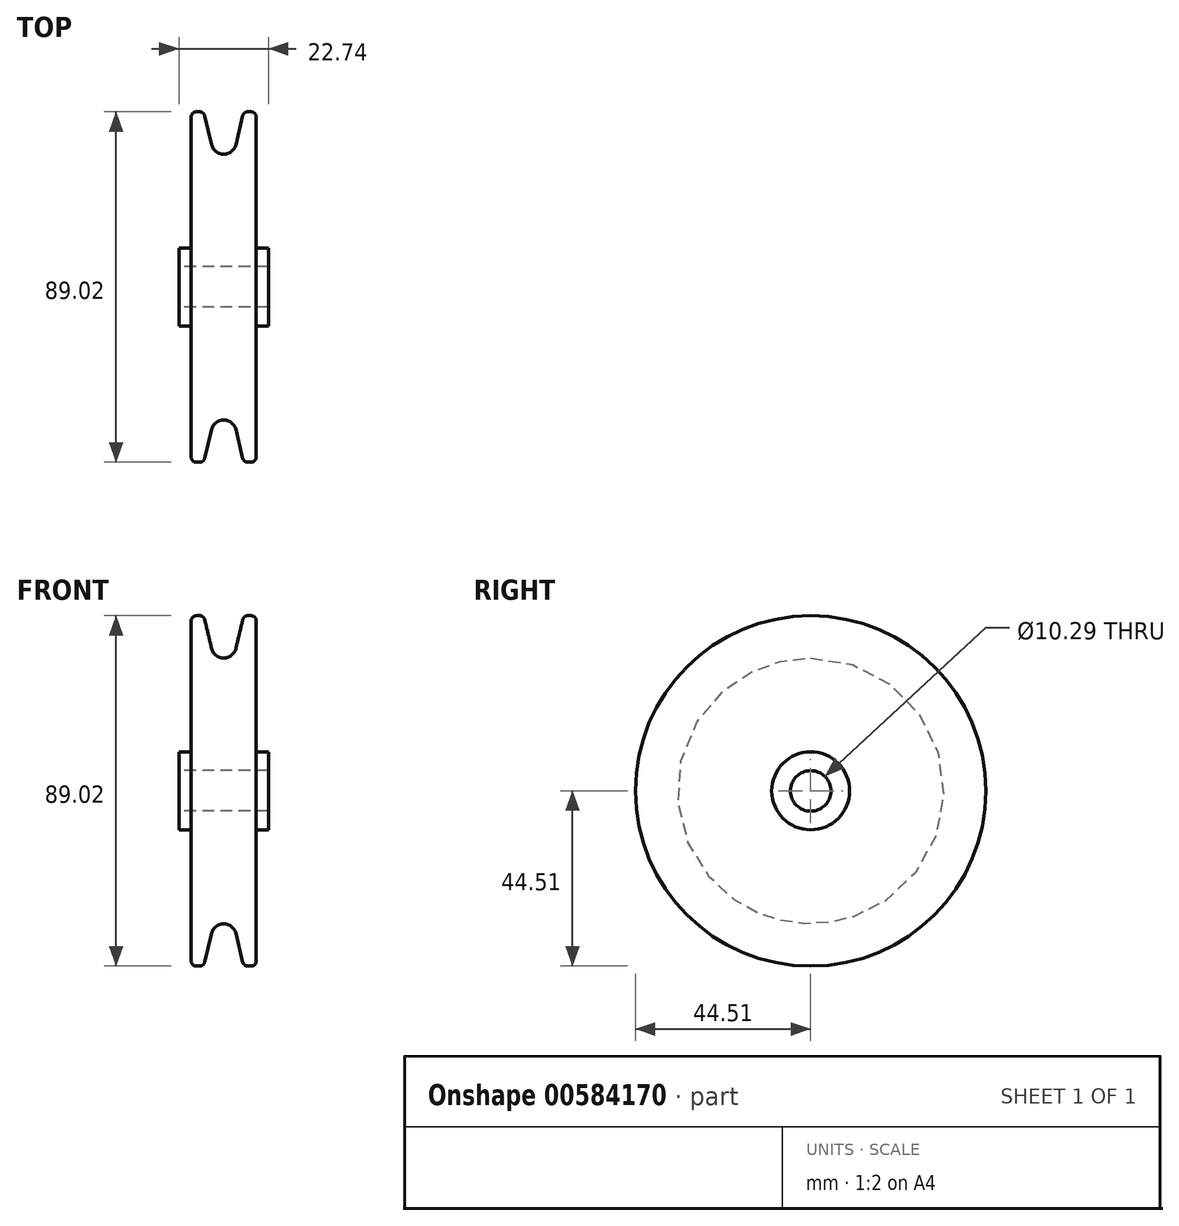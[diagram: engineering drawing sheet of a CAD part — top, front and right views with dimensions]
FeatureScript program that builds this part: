
annotation { "Feature Type Name" : "Feature", "Feature Type Description" : "" }
export const myFeature = defineFeature(function(context is Context, id is Id, definition is map)
    precondition{}
    {
        {
            var Q0;
            Q0=qCreatedBy(makeId("Front.planeOp"),FACE);
            var sketch = newSketch(context, id + "F0", { "sketchPlane" : qUnion([Q0])});
            skLineSegment(sketch, "E0", {"start": v(-11.37, 0) * mm, "end": v(11.37, 0) * mm, "construction": true});
            skLineSegment(sketch, "E1", {"start": v(-11.37, 5.14) * mm, "end": v(11.37, 5.14) * mm});
            skLineSegment(sketch, "E2", {"start": v(-11.37, 5.14) * mm, "end": v(-11.37, 9.9) * mm});
            skLineSegment(sketch, "E3", {"start": v(-11.37, 9.9) * mm, "end": v(-8.26, 9.9) * mm});
            skLineSegment(sketch, "E4", {"start": v(-8.26, 9.9) * mm, "end": v(-8.25, 44.51) * mm});
            skLineSegment(sketch, "E5", {"start": v(8.25, 44.51) * mm, "end": v(8.26, 9.9) * mm});
            skLineSegment(sketch, "E6", {"start": v(8.26, 9.9) * mm, "end": v(11.37, 9.9) * mm});
            skLineSegment(sketch, "E7", {"start": v(11.37, 9.9) * mm, "end": v(11.37, 5.14) * mm});
            skLineSegment(sketch, "E8", {"start": v(-8.25, 44.51) * mm, "end": v(-5.08, 44.51) * mm});
            skLineSegment(sketch, "E9", {"start": v(-5.08, 44.51) * mm, "end": v(-3.09, 36.22) * mm});
            skLineSegment(sketch, "E10", {"start": v(3.09, 36.22) * mm, "end": v(5.08, 44.51) * mm});
            skLineSegment(sketch, "E11", {"start": v(5.08, 44.51) * mm, "end": v(8.25, 44.51) * mm});
            skPoint(sketch, "E12.visualSharp", {"position": v(0, 23.36) * mm});
            skArc(sketch, "E12.filletArc", {"start": v(-3.09, 36.22) * mm, "mid": v(0, 33.78) * mm, "end": v(3.09, 36.22) * mm});
            skSolve(sketch);
        }
        {
            var Q0;
            Q0 = qSketchRegion(id + "F0", true);
            var Q1;
            Q1=sQuery(id+"F0.wireOp",EDGE,"E0");
            revolve(context, id + "F1", {"entities" : qUnion([Q0]), "axis" : qUnion([Q1]), "revolveType" : RevolveType.FULL});
        }
        {
            var Q0;
            Q0=makeQuery(id+"F1.opRevolve","SWEPT_FACE",FACE,{"disambiguationData":[OSD([sQuery(id+"F0.wireOp",EDGE,"E8")])]});
            var Q1;
            Q1=makeQuery(id+"F1.opRevolve","SWEPT_FACE",FACE,{"disambiguationData":[OSD([sQuery(id+"F0.wireOp",EDGE,"E11")])]});
            fillet(context, id + "F2", {"entities" : qUnion([Q0, Q1]), "radius" : 1.27 * mm, "tangentPropagation" : true, "allowEdgeOverflow" : false});
        }
    });
